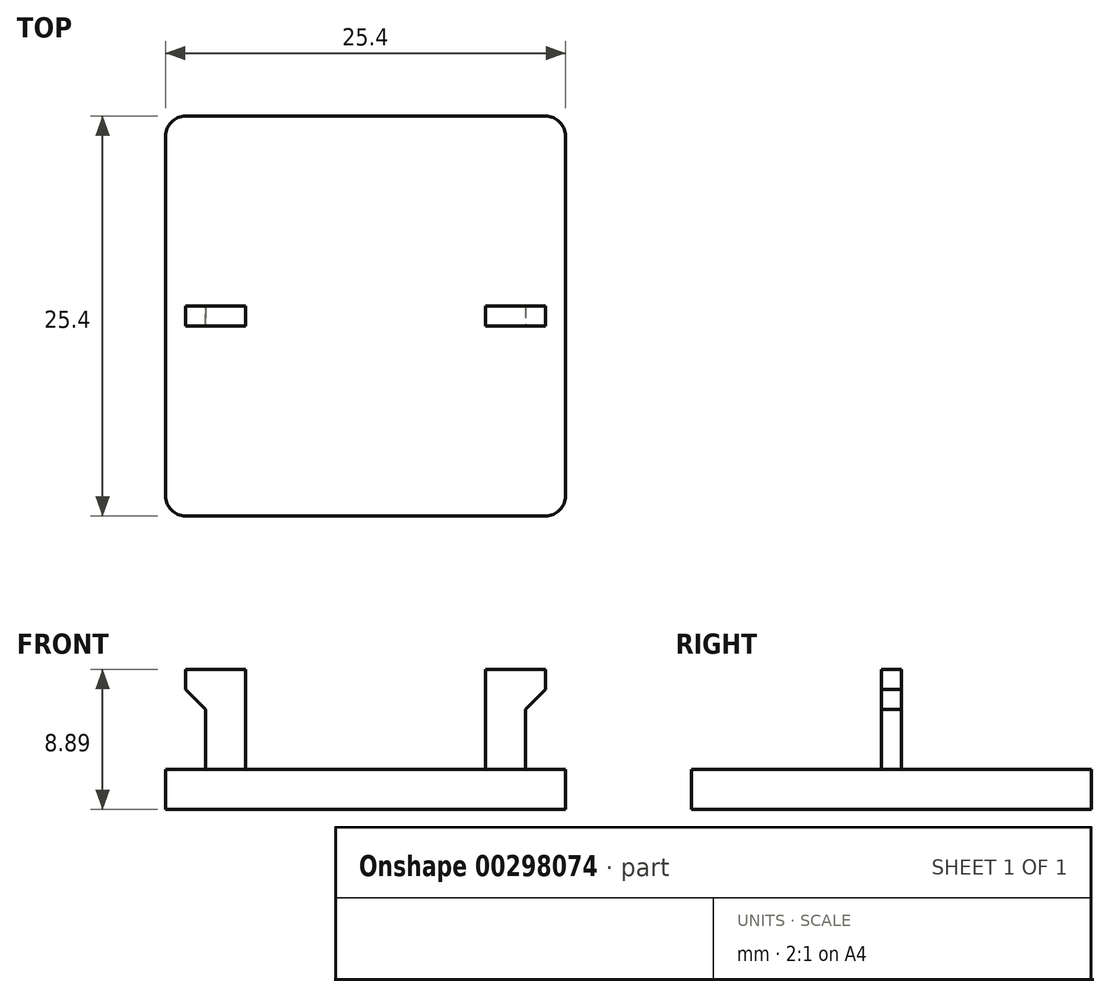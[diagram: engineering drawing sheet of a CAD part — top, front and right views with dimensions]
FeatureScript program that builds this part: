
annotation { "Feature Type Name" : "Feature", "Feature Type Description" : "" }
export const myFeature = defineFeature(function(context is Context, id is Id, definition is map)
    precondition{}
    {
        {
            var Q0;
            Q0=qCreatedBy(makeId("Top.planeOp"),FACE);
            var sketch = newSketch(context, id + "F0", { "sketchPlane" : qUnion([Q0])});
            skLineSegment(sketch, "E0.bottom", {"start": v(-12.7, 12.7) * mm, "end": v(12.7, 12.7) * mm});
            skLineSegment(sketch, "E0.top", {"start": v(-12.7, -12.7) * mm, "end": v(12.7, -12.7) * mm});
            skLineSegment(sketch, "E0.left", {"start": v(-12.7, 12.7) * mm, "end": v(-12.7, -12.7) * mm});
            skLineSegment(sketch, "E0.right", {"start": v(12.7, 12.7) * mm, "end": v(12.7, -12.7) * mm});
            skPoint(sketch, "E0.middle", {"position": v(0, 0) * mm});
            skLineSegment(sketch, "E1.bottom", {"start": v(-10.15, 0.63) * mm, "end": v(-7.6, 0.63) * mm});
            skLineSegment(sketch, "E1.top", {"start": v(-10.15, -0.64) * mm, "end": v(-7.6, -0.64) * mm});
            skLineSegment(sketch, "E1.left", {"start": v(-10.15, 0.63) * mm, "end": v(-10.15, -0.64) * mm});
            skLineSegment(sketch, "E1.right", {"start": v(-7.6, 0.63) * mm, "end": v(-7.6, -0.64) * mm});
            skPoint(sketch, "E1.middle", {"position": v(-8.88, 0) * mm});
            skLineSegment(sketch, "E2.bottom", {"start": v(10.15, 0.64) * mm, "end": v(7.6, 0.64) * mm});
            skLineSegment(sketch, "E2.top", {"start": v(10.15, -0.63) * mm, "end": v(7.6, -0.63) * mm});
            skLineSegment(sketch, "E2.left", {"start": v(10.15, 0.63) * mm, "end": v(10.15, -0.64) * mm});
            skLineSegment(sketch, "E2.right", {"start": v(7.6, 0.64) * mm, "end": v(7.6, -0.63) * mm});
            skPoint(sketch, "E2.middle", {"position": v(8.88, 0) * mm});
            skSolve(sketch);
        }
        {
            var Q0;
            Q0=makeQuery(id+"F0.imprint","IMPRINT",FACE,{"disambiguationData":[TD([[makeQuery(id+"F0.imprint","IMPRINT",EDGE,{"derivedFrom":sQuery(id+"F0.wireOp",EDGE,"E1.bottom")}),-1.0]])]});
            var Q1;
            Q1=makeQuery(id+"F0.imprint","IMPRINT",FACE,{"disambiguationData":[TD([[makeQuery(id+"F0.imprint","IMPRINT",EDGE,{"derivedFrom":sQuery(id+"F0.wireOp",EDGE,"E2.bottom")}),1.0]])]});
            extrude(context, id + "F1", {"entities" : qUnion([Q0, Q1]), "depth" : 8.9 * mm});
        }
        {
            var Q0;
            Q0 = qSketchRegion(id + "F0", true);
            extrude(context, id + "F2", {"entities" : qUnion([Q0]), "operationType" : NewBodyOperationType.ADD, "depth" : 2.54 * mm});
        }
        {
            var Q0;
            Q0=makeQuery(id+"F1.opExtrude","SWEPT_FACE",FACE,{"disambiguationData":[OSD([sQuery(id+"F0.wireOp",EDGE,"E1.left")])]});
            var sketch = newSketch(context, id + "F3", { "sketchPlane" : qUnion([Q0])});
            skLineSegment(sketch, "E3.bottom", {"start": v(0.63, 17.03) * mm, "end": v(-0.63, 17.03) * mm});
            skLineSegment(sketch, "E3.top", {"start": v(0.63, 14.73) * mm, "end": v(-0.63, 14.73) * mm});
            skLineSegment(sketch, "E3.left", {"start": v(0.63, 17.03) * mm, "end": v(0.63, 14.73) * mm});
            skLineSegment(sketch, "E3.right", {"start": v(-0.63, 17.03) * mm, "end": v(-0.63, 14.73) * mm});
            skPoint(sketch, "E3.middle", {"position": v(0, 15.88) * mm});
            skLineSegment(sketch, "E4.bottom", {"start": v(0.63, 8.9) * mm, "end": v(-0.63, 8.9) * mm});
            skLineSegment(sketch, "E4.top", {"start": v(0.63, 6.36) * mm, "end": v(-0.63, 6.36) * mm});
            skLineSegment(sketch, "E4.left", {"start": v(0.63, 8.9) * mm, "end": v(0.63, 6.36) * mm});
            skLineSegment(sketch, "E4.right", {"start": v(-0.63, 8.9) * mm, "end": v(-0.63, 6.36) * mm});
            skPoint(sketch, "E4.middle", {"position": v(0, 7.63) * mm});
            skSolve(sketch);
        }
        {
            var Q0;
            Q0=makeQuery(id+"F3.imprint","IMPRINT",FACE,{"disambiguationData":[TD([[makeQuery(id+"F3.imprint","IMPRINT",EDGE,{"derivedFrom":sQuery(id+"F3.wireOp",EDGE,"E4.bottom")}),-1.0]])]});
            extrude(context, id + "F4", {"entities" : qUnion([Q0]), "operationType" : NewBodyOperationType.ADD, "depth" : 1.27 * mm});
        }
        {
            var Q0;
            Q0=makeQuery(id+"F4.opExtrude","CAP_EDGE",EDGE,{"disambiguationData":[OSD([sQuery(id+"F3.wireOp",EDGE,"E4.top")])],"isStart":false});
            chamfer(context, id + "F5", {"entities" : qUnion([Q0]), "width" : 1.27 * mm, "tangentPropagation" : true});
        }
        {
            var Q0;
            Q0=makeQuery(id+"F1.opExtrude","SWEPT_FACE",FACE,{"disambiguationData":[OSD([sQuery(id+"F0.wireOp",EDGE,"E2.left")])]});
            var sketch = newSketch(context, id + "F6", { "sketchPlane" : qUnion([Q0])});
            skLineSegment(sketch, "E5.bottom", {"start": v(0.63, 6.36) * mm, "end": v(-0.63, 6.36) * mm});
            skLineSegment(sketch, "E5.top", {"start": v(0.63, 8.9) * mm, "end": v(-0.63, 8.9) * mm});
            skLineSegment(sketch, "E5.left", {"start": v(0.63, 6.36) * mm, "end": v(0.63, 8.9) * mm});
            skLineSegment(sketch, "E5.right", {"start": v(-0.63, 6.36) * mm, "end": v(-0.63, 8.9) * mm});
            skPoint(sketch, "E5.middle", {"position": v(0, 7.63) * mm});
            skPoint(sketch, "E5.middle.positionSnap0", {"position": v(0, 8.9) * mm});
            skPoint(sketch, "E5.centerSnap0", {"position": v(0, 8.9) * mm});
            skSolve(sketch);
        }
        {
            var Q0;
            Q0=makeQuery(id+"F6.imprint","IMPRINT",FACE,{"disambiguationData":[TD([[makeQuery(id+"F6.imprint","IMPRINT",EDGE,{"derivedFrom":sQuery(id+"F6.wireOp",EDGE,"E5.bottom")}),-1.0]])]});
            extrude(context, id + "F7", {"entities" : qUnion([Q0]), "operationType" : NewBodyOperationType.ADD, "depth" : 1.27 * mm});
        }
        {
            var Q0;
            Q0=makeQuery(id+"F7.opExtrude","CAP_EDGE",EDGE,{"disambiguationData":[OSD([sQuery(id+"F6.wireOp",EDGE,"E5.bottom")])],"isStart":false});
            chamfer(context, id + "F8", {"entities" : qUnion([Q0]), "width" : 1.27 * mm, "tangentPropagation" : true});
        }
        {
            var Q0;
            Q0=makeQuery(id+"F2.opExtrude","SWEPT_EDGE",EDGE,{"disambiguationData":[OSD([sQuery(id+"F0.wireOp",EDGE,"E0.top"),sQuery(id+"F0.wireOp",EDGE,"E0.right")])]});
            var Q1;
            Q1=makeQuery(id+"F2.opExtrude","SWEPT_EDGE",EDGE,{"disambiguationData":[OSD([sQuery(id+"F0.wireOp",EDGE,"E0.bottom"),sQuery(id+"F0.wireOp",EDGE,"E0.right")])]});
            var Q2;
            Q2=makeQuery(id+"F2.opExtrude","SWEPT_EDGE",EDGE,{"disambiguationData":[OSD([sQuery(id+"F0.wireOp",EDGE,"E0.top"),sQuery(id+"F0.wireOp",EDGE,"E0.left")])]});
            var Q3;
            Q3=makeQuery(id+"F2.opExtrude","SWEPT_EDGE",EDGE,{"disambiguationData":[OSD([sQuery(id+"F0.wireOp",EDGE,"E0.bottom"),sQuery(id+"F0.wireOp",EDGE,"E0.left")])]});
            fillet(context, id + "F9", {"entities" : qUnion([Q0, Q1, Q2, Q3]), "radius" : 1.27 * mm, "tangentPropagation" : true, "allowEdgeOverflow" : false});
        }
    });
